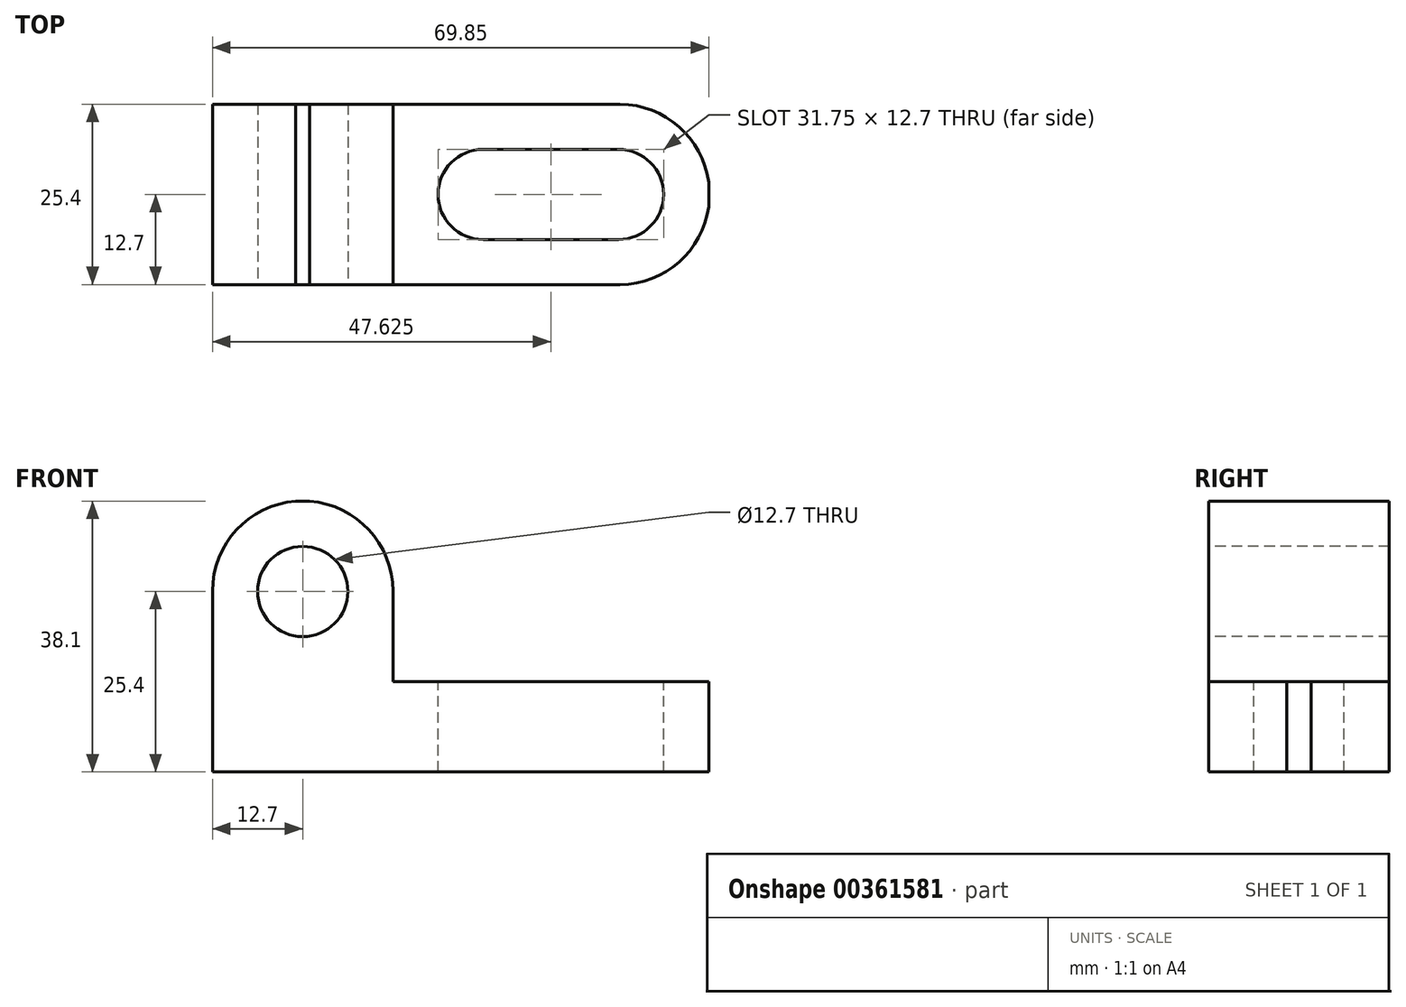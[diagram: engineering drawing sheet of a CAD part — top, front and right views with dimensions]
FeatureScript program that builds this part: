
annotation { "Feature Type Name" : "Feature", "Feature Type Description" : "" }
export const myFeature = defineFeature(function(context is Context, id is Id, definition is map)
    precondition{}
    {
        {
            var Q0;
            Q0=qCreatedBy(makeId("Front.planeOp"),FACE);
            var sketch = newSketch(context, id + "F0", { "sketchPlane" : qUnion([Q0])});
            skLineSegment(sketch, "E0", {"start": v(0, 0) * mm, "end": v(69.85, 0) * mm});
            skLineSegment(sketch, "E1", {"start": v(69.85, 0) * mm, "end": v(69.85, 12.7) * mm});
            skLineSegment(sketch, "E2", {"start": v(69.85, 12.7) * mm, "end": v(25.4, 12.7) * mm});
            skLineSegment(sketch, "E3", {"start": v(25.4, 12.7) * mm, "end": v(25.4, 38.1) * mm});
            skLineSegment(sketch, "E4", {"start": v(25.4, 38.1) * mm, "end": v(0, 38.1) * mm});
            skLineSegment(sketch, "E5", {"start": v(0, 38.1) * mm, "end": v(0, 0) * mm});
            skSolve(sketch);
        }
        {
            var Q0;
            Q0=makeQuery(id+"F0.imprint","IMPRINT",FACE,{"disambiguationData":[TD([[makeQuery(id+"F0.imprint","IMPRINT",EDGE,{"derivedFrom":sQuery(id+"F0.wireOp",EDGE,"E0")}),1.0]])]});
            extrude(context, id + "F1", {"entities" : qUnion([Q0]), "depth" : 25.4 * mm});
        }
        {
            var Q0;
            Q0=makeQuery(id+"F1.opExtrude","CAP_FACE",FACE,{"disambiguationData":[OSD([sQuery(id+"F0.wireOp",EDGE,"E0"),sQuery(id+"F0.wireOp",EDGE,"E1"),sQuery(id+"F0.wireOp",EDGE,"E2"),sQuery(id+"F0.wireOp",EDGE,"E3"),sQuery(id+"F0.wireOp",EDGE,"E4"),sQuery(id+"F0.wireOp",EDGE,"E5")])],"isStart":false});
            var sketch = newSketch(context, id + "F2", { "sketchPlane" : qUnion([Q0])});
            skCircle(sketch, "E6", {"center": v(12.7, 25.4) * mm, "radius": 6.35 * mm});
            skPoint(sketch, "E6.centerSnap0", {"position": v(12.7, 38.1) * mm});
            skArc(sketch, "E7", {"start": v(25.4, 25.4) * mm, "mid": v(12.7, 38.14) * mm, "end": v(0, 25.4) * mm});
            skSolve(sketch);
        }
        {
            var Q0;
            Q0=makeQuery(id+"F2.imprint","IMPRINT",FACE,{"disambiguationData":[TD([[makeQuery(id+"F2.imprint","IMPRINT",EDGE,{"derivedFrom":sQuery(id+"F2.wireOp",EDGE,"E6")}),1.0]])]});
            var Q1;
            {var subQ0=sQuery(id+"F2.wireOp",EDGE,"E7");var subQ1=makeQuery(id+"F1.opExtrude","CAP_EDGE",EDGE,{"disambiguationData":[OSD([sQuery(id+"F0.wireOp",EDGE,"E5")])],"isStart":false});var subQ2=makeQuery(id+"F2.imprint","INTERSECT",VERTEX,{"derivedFrom":[subQ1,subQ0]});Q1=makeQuery(id+"F2.imprint","IMPRINT",FACE,{"disambiguationData":[TD([[makeQuery(id+"F2.imprint","IMPRINT",EDGE,{"disambiguationData":[TD([[subQ2,1.0]])],"derivedFrom":subQ0}),-1.0]])]});}
            var Q2;
            {var subQ0=sQuery(id+"F2.wireOp",EDGE,"E7");var subQ1=makeQuery(id+"F1.opExtrude","CAP_EDGE",EDGE,{"disambiguationData":[OSD([sQuery(id+"F0.wireOp",EDGE,"E3")])],"isStart":false});var subQ2=makeQuery(id+"F2.imprint","INTERSECT",VERTEX,{"derivedFrom":[subQ1,subQ0]});Q2=makeQuery(id+"F2.imprint","IMPRINT",FACE,{"disambiguationData":[TD([[makeQuery(id+"F2.imprint","IMPRINT",EDGE,{"disambiguationData":[TD([[subQ2,-1.0]])],"derivedFrom":subQ0}),-1.0]])]});}
            extrude(context, id + "F3", {"entities" : qUnion([Q0, Q1, Q2]), "operationType" : NewBodyOperationType.REMOVE, "oppositeDirection" : true, "depth" : 25.4 * mm});
        }
        {
            var Q0;
            Q0=makeQuery(id+"F1.opExtrude","SWEPT_FACE",FACE,{"disambiguationData":[OSD([sQuery(id+"F0.wireOp",EDGE,"E2")])]});
            var sketch = newSketch(context, id + "F4", { "sketchPlane" : qUnion([Q0])});
            skCircle(sketch, "E8", {"center": v(38.1, -12.7) * mm, "radius": 6.35 * mm});
            skCircle(sketch, "E9", {"center": v(57.15, -12.7) * mm, "radius": 6.35 * mm});
            skArc(sketch, "E10", {"start": v(57.15, -25.4) * mm, "mid": v(69.97, -12.7) * mm, "end": v(57.15, 0) * mm});
            skSolve(sketch);
        }
        {
            var Q0;
            Q0=makeQuery(id+"F4.imprint","IMPRINT",FACE,{"disambiguationData":[TD([[makeQuery(id+"F4.imprint","IMPRINT",EDGE,{"derivedFrom":sQuery(id+"F4.wireOp",EDGE,"E8")}),1.0]])]});
            var Q1;
            Q1=makeQuery(id+"F4.imprint","IMPRINT",FACE,{"disambiguationData":[TD([[makeQuery(id+"F4.imprint","IMPRINT",EDGE,{"derivedFrom":sQuery(id+"F4.wireOp",EDGE,"E9")}),1.0]])]});
            var Q2;
            {var subQ0=sQuery(id+"F4.wireOp",EDGE,"E10");var subQ1=sQuery(id+"F0.wireOp",EDGE,"E2");var subQ4=makeQuery(id+"F1.opExtrude","CAP_EDGE",EDGE,{"disambiguationData":[OSD([subQ1])],"isStart":true});var subQ5=makeQuery(id+"F4.imprint","INTERSECT",VERTEX,{"disambiguationData":[OD(1.0)],"derivedFrom":[subQ4,subQ0]});Q2=makeQuery(id+"F4.imprint","IMPRINT",FACE,{"disambiguationData":[TD([[makeQuery(id+"F4.imprint","IMPRINT",EDGE,{"disambiguationData":[TD([[subQ5,1.0]])],"derivedFrom":subQ0}),-1.0]])]});}
            var Q3;
            {var subQ0=sQuery(id+"F4.wireOp",EDGE,"E10");var subQ1=sQuery(id+"F0.wireOp",EDGE,"E2");var subQ2=makeQuery(id+"F1.opExtrude","CAP_EDGE",EDGE,{"disambiguationData":[OSD([subQ1])],"isStart":false});var subQ3=makeQuery(id+"F4.imprint","INTERSECT",VERTEX,{"disambiguationData":[OD(1.0)],"derivedFrom":[subQ2,subQ0]});Q3=makeQuery(id+"F4.imprint","IMPRINT",FACE,{"disambiguationData":[TD([[makeQuery(id+"F4.imprint","IMPRINT",EDGE,{"disambiguationData":[TD([[subQ3,-1.0]])],"derivedFrom":subQ0}),-1.0]])]});}
            extrude(context, id + "F5", {"entities" : qUnion([Q0, Q1, Q2, Q3]), "operationType" : NewBodyOperationType.REMOVE, "oppositeDirection" : true, "depth" : 12.7 * mm});
        }
        {
            var Q0;
            Q0=makeQuery(id+"F1.opExtrude","SWEPT_FACE",FACE,{"disambiguationData":[OSD([sQuery(id+"F0.wireOp",EDGE,"E2")])]});
            var sketch = newSketch(context, id + "F6", { "sketchPlane" : qUnion([Q0])});
            skLineSegment(sketch, "E11", {"start": v(38.1, -6.35) * mm, "end": v(57.15, -6.35) * mm});
            skLineSegment(sketch, "E12", {"start": v(38.1, -19.05) * mm, "end": v(57.15, -19.05) * mm});
            skSolve(sketch);
        }
        {
            var Q0;
            {var subQ0=sQuery(id+"F6.wireOp",EDGE,"E11");Q0=makeQuery(id+"F6.imprint","IMPRINT",FACE,{"disambiguationData":[TD([[makeQuery(id+"F6.imprint","IMPRINT",EDGE,{"derivedFrom":subQ0}),-1.0]])]});}
            extrude(context, id + "F7", {"entities" : qUnion([Q0]), "operationType" : NewBodyOperationType.REMOVE, "oppositeDirection" : true, "depth" : 12.7 * mm});
        }
    });
